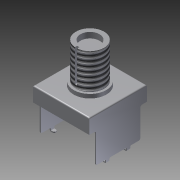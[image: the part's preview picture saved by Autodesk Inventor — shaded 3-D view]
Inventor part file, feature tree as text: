
AUTODESK INVENTOR PART (.ipt)
format: ipt  version: 2011 SP1 (Build 150282100, 282)  size: 235,520 bytes
history: native  units: in
note: dims shown in document units (in); Inventor stores cm internally (conversion verified against a paired STEP export)
features: other x56, sketch x11, extrude x7, revolve x4, thread x1
ambient origin geometry x8: Origin, YZ Plane, XZ Plane, XY Plane, X Axis, Y Axis, Z Axis, Center Point
bodies: Solid1 (feature_tree), body_c_to_bracket_XY (feature_tree), body_c_to_bracket_YZ (feature_tree), body_c_to_bracket_ZX (feature_tree), body_c_to_bracket_X (feature_tree), body_c_to_bracket_Y (feature_tree), body_c_to_bracket_Z (feature_tree), body_c_to_bracket_Center (feature_tree), body_cover_to_body_XY (feature_tree), body_cover_to_body_YZ (feature_tree), body_cover_to_body_ZX (feature_tree), body_cover_to_body_X (feature_tree), body_cover_to_body_Y (feature_tree), body_cover_to_body_Z (feature_tree), body_cover_to_body_Center (feature_tree), body_cover_to_toggle_XY (feature_tree), body_cover_to_toggle_YZ (feature_tree), body_cover_to_toggle_ZX (feature_tree), body_cover_to_toggle_X (feature_tree), body_cover_to_toggle_Y (feature_tree), body_cover_to_toggle_Z (feature_tree), body_cover_to_toggle_Center (feature_tree), body_cover_to_toggle2_XY (feature_tree), body_cover_to_toggle2_YZ (feature_tree), body_cover_to_toggle2_ZX (feature_tree), body_cover_to_toggle2_X (feature_tree), body_cover_to_toggle2_Y (feature_tree), body_cover_to_toggle2_Z (feature_tree), body_cover_to_toggle2_Center (feature_tree)
feature tree (79):
  extrude  "Extrusion1"  Depth=0.504in TaperAngle=0.0deg
  extrude  "Extrusion2"  TaperAngle=90.0deg  [1 undecoded]
  extrude  "Extrusion3"  Depth=0.01in TaperAngle=0.0deg
  revolve  "Revolution1"  [1 undecoded]
  revolve  "Revolution2"  [1 undecoded]
  extrude  "Extrusion4"  Depth=0.8in TaperAngle=0.0deg
  extrude  "Extrusion5"  [1 undecoded]
  extrude  "Extrusion6"  [1 undecoded]
  revolve  "Revolution3"  [1 undecoded]
  thread  "Thread1"  [1 undecoded]
  revolve  "Revolution4"  [1 undecoded]
  extrude  "Extrusion7"  [1 undecoded]
  other  "at507h_XY"
  other  "at507h_YZ"
  other  "at507h_ZX"
  other  "at507h_X"
  other  "at507h_Y"
  other  "at507h_Z"
  other  "at507h_Center"
  other  "at507h_dual_XY"
  other  "at507h_dual_YZ"
  other  "at507h_dual_ZX"
  other  "at507h_dual_X"
  other  "at507h_dual_Y"
  other  "at507h_dual_Z"
  other  "at507h_dual_Center"
  other  "at509_XY"
  other  "at509_YZ"
  other  "at509_ZX"
  other  "at509_X"
  other  "at509_Y"
  other  "at509_Z"
  other  "at509_Center"
  other  "at509_dual_XY"
  other  "at509_dual_YZ"
  other  "at509_dual_ZX"
  other  "at509_dual_X"
  other  "at509_dual_Y"
  other  "at509_dual_Z"
  other  "at509_dual_Center"
  other  "at513h_XY"
  other  "at513h_YZ"
  other  "at513h_ZX"
  other  "at513h_X"
  other  "at513h_Y"
  other  "at513h_Z"
  other  "at513h_Center"
  other  "at513h_dual_XY"
  other  "at513h_dual_YZ"
  other  "at513h_dual_ZX"
  other  "at513h_dual_X"
  other  "at513h_dual_Y"
  other  "at513h_dual_Z"
  other  "at513h_dual_Center"
  other  "st513h_2_XY"
  other  "st513h_2_YZ"
  other  "st513h_2_ZX"
  other  "st513h_2_X"
  other  "st513h_2_Y"
  other  "st513h_2_Z"
  other  "st513h_2_Center"
  other  "st513h_2_dual_XY"
  other  "st513h_2_dual_YZ"
  other  "st513h_2_dual_ZX"
  other  "st513h_2_dual_X"
  other  "st513h_2_dual_Y"
  other  "st513h_2_dual_Z"
  other  "st513h_2_dual_Center"
  sketch  "Sketch_1"  dims[d0=0.5in d1=0.0in d2=0.504in d3=0.0in]
  sketch  "Sketch_2"  dims[d4=1.008in d5=0.0in d6=90.0deg]
  sketch  "Sketch_3"  dims[d7=90.0deg d8=0.01in d9=0.0in]
  sketch  "Sketch_4"  dims[d10=0.01in d11=0.0in d12=1.0in d13=0.0in]
  sketch  "Sketch_5"  dims[d14=360.0deg d15=0.315in d16=0.0in]
  sketch  "Sketch_6"  dims[d17=360.0deg d18=0.8in d19=0.0in]
  sketch  "Sketch_7"
  sketch  "Sketch_8"
  sketch  "Sketch_17"
  sketch  "Sketch_19"
  sketch  "Sketch_35"
note: 9 required parameter values undecoded (feature->parameter linkage not recoverable at this tier; creation-order binding heuristic only, values carry confidence <= 0.55)